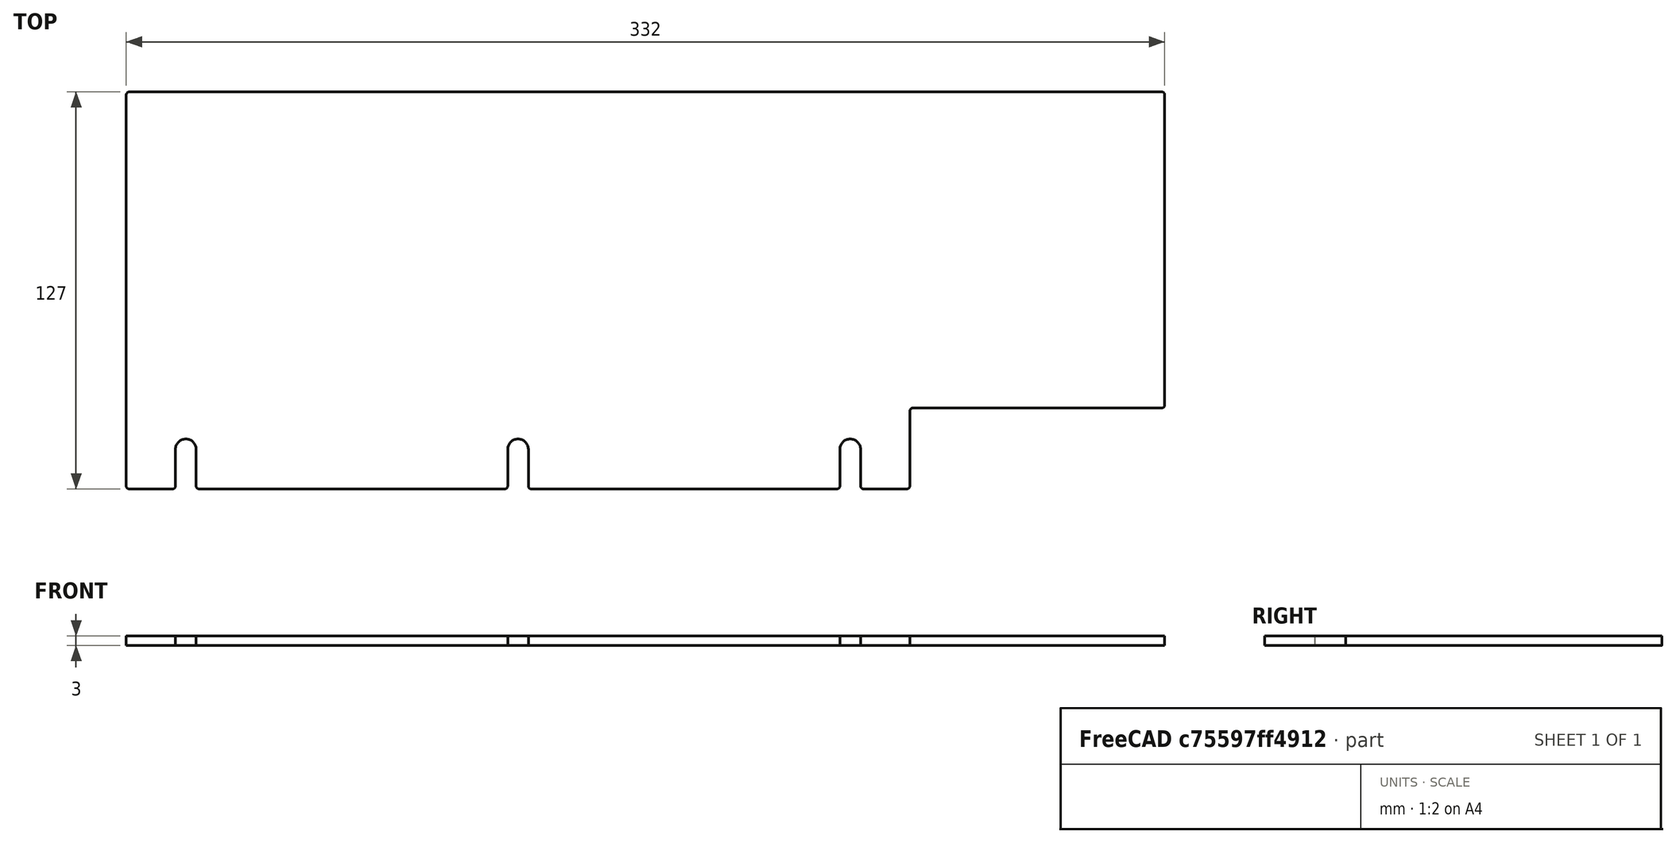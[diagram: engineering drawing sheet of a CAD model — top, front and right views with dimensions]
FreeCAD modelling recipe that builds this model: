
FCSTD DOCUMENT  (FreeCAD 0.21R33675 (Git))
Label: right_wall_front_5in
License: All rights reserved
LicenseURL: http://en.wikipedia.org/wiki/All_rights_reserved
objects: Spreadsheet::Sheet×1, Sketcher::SketchObject×1, PartDesign::Pad×1, PartDesign::Body×1
note: 4 computed .brp shape members not serialized (recipe doc carries the construction recipe); baked Part::Feature solids carry a one-line shape summary decoded from their .brp

FEATURE [Spreadsheet::Sheet] Spreadsheet
  cells = A2='Parameters; A3='ServoOffsetFromCenter; B3(ServoOffsetFromCenter)==-3 in; A4='BeamLength; B4(BeamLength)==18 in; A5='BracketLength; B5(BracketLength)==108.6 mm; A6='DistanceLeftBracketEdgeToDoor; B6(DistanceLeftBracketEdgeToDoor)==82.4999 mm; A7='DistanceRightBracketEdgeToDoor; B7(DistanceRightBracketEdgeToDoor)==23.1001 mm; A8='DoorMargin; B8(DoorMargin)==1 mm; A9='LengthMargin; B9(LengthMargin)==0 mm; A10='LengthLeftBracketEdgeToDoorGap; B10(LengthLeftBracketEdgeToDoorGap)==DistanceLeftBracketEdgeToDoor - DoorMargin; A11='LengthRightBracketEdgeToDoorGap; B11(LengthRightBracketEdgeToDoorGap)==DistanceRightBracketEdgeToDoor - DoorMargin; A12='LengthDoorGap; B12(LengthDoorGap)==BracketLength - LengthLeftBracketEdgeToDoorGap - LengthRightBracketEdgeToDoorGap; A13='BeamLengthMinusBracketLength; B13(BeamLengthMinusBracketLength)==BeamLength - BracketLength; A14='DistanceFrontToDoor; B14(DistanceFrontToDoor)==0.5 * BeamLengthMinusBracketLength + LengthLeftBracketEdgeToDoorGap - ServoOffsetFromCenter; A15='DistanceFrontToBracket; B15(DistanceFrontToBracket)==0.5 * BeamLengthMinusBracketLength - ServoOffsetFromCenter; A16='LengthFrontToDoor; B16(LengthFrontToDoor)==DistanceFrontToDoor - LengthMargin; A17='LengthFrontToBracket; B17(LengthFrontToBracket)==DistanceFrontToBracket - LengthMargin; A18='Height; B18(Height)==5 in; A19='Thickness; B19(Thickness)==3 mm; A20='CutoutMargin; B20(CutoutMargin)==0.5 mm; A21='CutoutHeight; B21(CutoutHeight)==1 in + CutoutMargin; A22='FilletRadius; B22(FilletRadius)==1 mm; A23='MountHoleDiameter; B23(MountHoleDiameter)==0.26 in; A24='MountHoleDistanceFromBottom; B24(MountHoleDistanceFromBottom)==0.5 in; A25='MountHoleSideMargin; B25(MountHoleSideMargin)==0.75 in
FEATURE [Sketcher::SketchObject] Sketch
  FullyConstrained = true
  MapMode = 5
  Support = -> [XY_Plane]
  expr: Constraints[14] = Spreadsheet.FilletRadius
  expr: Constraints[20] = Spreadsheet.Height
  expr: Constraints[43] = Spreadsheet.MountHoleDistanceFromBottom
  expr: Constraints[44] = Spreadsheet.MountHoleDiameter
  expr: Constraints[64] = Spreadsheet.MountHoleSideMargin
  expr: Constraints[7] = Spreadsheet.LengthFrontToDoor
  expr: Constraints[8] = Spreadsheet.LengthFrontToBracket
  expr: Constraints[9] = Spreadsheet.CutoutHeight
  sketch-geometry (50):
    g0: LineSegment StartX=0 StartY=126 StartZ=0 EndX=0 EndY=1 EndZ=0
    g1: LineSegment StartX=1 StartY=0 StartZ=0 EndX=249.5 EndY=0 EndZ=0
    g2: LineSegment StartX=250.5 StartY=1 StartZ=0 EndX=250.5 EndY=24.9 EndZ=0
    g3: LineSegment StartX=251.5 StartY=25.9 StartZ=0 EndX=331 EndY=25.9 EndZ=0
    g4: LineSegment StartX=332 StartY=26.9 StartZ=0 EndX=332 EndY=126 EndZ=0
    g5: LineSegment StartX=331 StartY=127 StartZ=0 EndX=1 EndY=127 EndZ=0
    g6: ArcOfCircle CenterX=1 CenterY=126 CenterZ=0 NormalX=0 NormalY=0 NormalZ=1 AngleXU=0 Radius=1 StartAngle=1.5708 EndAngle=3.14159
    g7: GeomPoint X=0 Y=127 Z=0
    g8: ArcOfCircle CenterX=1 CenterY=1 CenterZ=0 NormalX=0 NormalY=0 NormalZ=1 AngleXU=0 Radius=1 StartAngle=3.14159 EndAngle=4.71239
    g9: GeomPoint X=0 Y=0 Z=0
    g10: ArcOfCircle CenterX=249.5 CenterY=1 CenterZ=0 NormalX=0 NormalY=0 NormalZ=1 AngleXU=0 Radius=1 StartAngle=4.71239 EndAngle=6.28319
    g11: GeomPoint X=250.5 Y=0 Z=0
    g12: ArcOfCircle CenterX=251.5 CenterY=24.9 CenterZ=0 NormalX=0 NormalY=0 NormalZ=1 AngleXU=0 Radius=1 StartAngle=1.5708 EndAngle=3.14159
    g13: GeomPoint X=250.5 Y=25.9 Z=0
    g14: ArcOfCircle CenterX=331 CenterY=26.9 CenterZ=0 NormalX=0 NormalY=0 NormalZ=1 AngleXU=0 Radius=1 StartAngle=4.71239 EndAngle=6.28319
    g15: GeomPoint X=332 Y=25.9 Z=0
    g16: ArcOfCircle CenterX=331 CenterY=126 CenterZ=0 NormalX=0 NormalY=0 NormalZ=1 AngleXU=0 Radius=1 StartAngle=-1.8e-15 EndAngle=1.5708
    g17: GeomPoint X=332 Y=127 Z=0
    g18: GeomPoint X=125.25 Y=0 Z=0
    g19: LineSegment StartX=125.25 StartY=0 StartZ=0 EndX=125.25 EndY=12.7 EndZ=0
    g20: Circle CenterX=125.25 CenterY=12.7 CenterZ=0 NormalX=0 NormalY=0 NormalZ=1 AngleXU=0 Radius=3.302
    g21: LineSegment StartX=19.05 StartY=0 StartZ=0 EndX=19.05 EndY=12.7 EndZ=0
    g22: LineSegment StartX=231.45 StartY=0 StartZ=0 EndX=231.45 EndY=12.7 EndZ=0
    g23: Circle CenterX=19.05 CenterY=12.7 CenterZ=0 NormalX=0 NormalY=0 NormalZ=1 AngleXU=0 Radius=3.302
    g24: Circle CenterX=231.45 CenterY=12.7 CenterZ=0 NormalX=0 NormalY=0 NormalZ=1 AngleXU=0 Radius=3.302
    g25: LineSegment StartX=19.05 StartY=12.7 StartZ=0 EndX=0 EndY=12.7 EndZ=0
    g26: LineSegment StartX=231.45 StartY=12.7 StartZ=0 EndX=250.5 EndY=12.7 EndZ=0
    g27: ArcOfCircle CenterX=19.05 CenterY=12.7 CenterZ=0 NormalX=0 NormalY=0 NormalZ=1 AngleXU=0 Radius=3.302 StartAngle=0 EndAngle=3.14159
    g28: LineSegment StartX=19.05 StartY=12.7 StartZ=0 EndX=22.352 EndY=12.7 EndZ=0
    g29: LineSegment StartX=15.748 StartY=12.7 StartZ=0 EndX=15.748 EndY=1 EndZ=0
    g30: LineSegment StartX=22.352 StartY=12.7 StartZ=0 EndX=22.352 EndY=1 EndZ=0
    g31: ArcOfCircle CenterX=14.748 CenterY=1 CenterZ=0 NormalX=0 NormalY=0 NormalZ=1 AngleXU=0 Radius=1 StartAngle=4.71239 EndAngle=6.28319
    g32: ArcOfCircle CenterX=23.352 CenterY=1 CenterZ=0 NormalX=0 NormalY=0 NormalZ=1 AngleXU=0 Radius=1 StartAngle=3.14159 EndAngle=4.71239
    g33: LineSegment StartX=121.948 StartY=12.7 StartZ=0 EndX=121.948 EndY=1 EndZ=0
    g34: LineSegment StartX=128.552 StartY=12.7 StartZ=0 EndX=128.552 EndY=1 EndZ=0
    g35: ArcOfCircle CenterX=120.948 CenterY=1 CenterZ=0 NormalX=0 NormalY=0 NormalZ=1 AngleXU=0 Radius=1 StartAngle=4.71239 EndAngle=6.28319
    g36: ArcOfCircle CenterX=129.552 CenterY=1 CenterZ=0 NormalX=0 NormalY=0 NormalZ=1 AngleXU=0 Radius=1 StartAngle=3.14159 EndAngle=4.71239
    g37: ArcOfCircle CenterX=125.25 CenterY=12.7 CenterZ=0 NormalX=0 NormalY=0 NormalZ=1 AngleXU=0 Radius=3.302 StartAngle=-7.1e-15 EndAngle=3.14159
    g38: LineSegment StartX=125.25 StartY=12.7 StartZ=0 EndX=121.948 EndY=12.7 EndZ=0
    g39: LineSegment StartX=125.25 StartY=12.7 StartZ=0 EndX=128.552 EndY=12.7 EndZ=0
    g40: LineSegment StartX=228.148 StartY=12.7 StartZ=0 EndX=228.148 EndY=1 EndZ=0
    g41: LineSegment StartX=234.752 StartY=12.7 StartZ=0 EndX=234.752 EndY=1 EndZ=0
    g42: ArcOfCircle CenterX=227.148 CenterY=1 CenterZ=0 NormalX=0 NormalY=0 NormalZ=1 AngleXU=0 Radius=1 StartAngle=4.71239 EndAngle=6.28319
    g43: ArcOfCircle CenterX=235.752 CenterY=1 CenterZ=0 NormalX=0 NormalY=0 NormalZ=1 AngleXU=0 Radius=1 StartAngle=3.14159 EndAngle=4.71239
    g44: ArcOfCircle CenterX=231.45 CenterY=12.7 CenterZ=0 NormalX=0 NormalY=0 NormalZ=1 AngleXU=0 Radius=3.302 StartAngle=1.2e-15 EndAngle=3.14159
    g45: LineSegment StartX=231.45 StartY=12.7 StartZ=0 EndX=228.148 EndY=12.7 EndZ=0
    g46: LineSegment StartX=1 StartY=0 StartZ=0 EndX=14.748 EndY=0 EndZ=0
    g47: LineSegment StartX=23.352 StartY=0 StartZ=0 EndX=120.948 EndY=0 EndZ=0
    g48: LineSegment StartX=129.552 StartY=0 StartZ=0 EndX=227.148 EndY=0 EndZ=0
    g49: LineSegment StartX=235.752 StartY=0 StartZ=0 EndX=249.5 EndY=0 EndZ=0
  constraints (126):
    c: Vertical(g0)
    c: Horizontal(g1)
    c: Vertical(g2)
    c: Horizontal(g3)
    c: Vertical(g4)
    c: Horizontal(g5)
    c: Coincident(g-1,g9)
    c: DistanceX(g7,g17) = 332
    c: DistanceX(g9,g11) = 250.5
    c: DistanceY(g11,g13) = 25.9
    c: PointOnObject(g7,g0)
    c: PointOnObject(g7,g5)
    c: Tangent(g0,g6) = -1.5708
    c: Tangent(g5,g6) = -1.5708
    c: Radius(g6) = 1
    c: PointOnObject(g9,g0)
    c: PointOnObject(g9,g1)
    c: Tangent(g0,g8) = -1.5708
    c: Tangent(g1,g8) = -1.5708
    c: Equal(g8,g6)
    c: DistanceY(g1,g5) = 127
    c: PointOnObject(g11,g1)
    c: PointOnObject(g11,g2)
    c: Tangent(g1,g10) = -1.5708
    c: Tangent(g2,g10) = -1.5708
    c: Equal(g10,g8)
    c: PointOnObject(g13,g2)
    c: PointOnObject(g13,g3)
    c: Tangent(g2,g12) = 1.5708
    c: Tangent(g3,g12) = 1.5708
    c: Equal(g12,g10)
    c: PointOnObject(g15,g3)
    c: PointOnObject(g15,g4)
    c: Tangent(g3,g14) = -1.5708
    c: Tangent(g4,g14) = -1.5708
    c: Equal(g14,g12)
    c: PointOnObject(g17,g5)
    c: PointOnObject(g17,g4)
    c: Tangent(g5,g16) = -1.5708
    c: Tangent(g4,g16) = -1.5708
    c: Equal(g16,g14)
    c: Coincident(g19,g18)
    c: Vertical(g19)
    c: DistanceY(g19,g19) = 12.7
    c: Diameter(g20) = 6.604
    c: Coincident(g19,g20)
    c: Symmetric(g1,g1,g18)
    c: Vertical(g21)
    c: Vertical(g22)
    c: PointOnObject(g21,g1)
    c: PointOnObject(g22,g1)
    c: Equal(g21,g19)
    c: Equal(g19,g22)
    c: Equal(g23,g20)
    c: Equal(g20,g24)
    c: Coincident(g23,g21)
    c: Coincident(g24,g22)
    c: Coincident(g25,g23)
    c: PointOnObject(g25,g0)
    c: Horizontal(g25)
    c: Coincident(g26,g24)
    c: PointOnObject(g26,g2)
    c: Horizontal(g26)
    c: Equal(g25,g26)
    c: DistanceX(g25,g25) = 19.05
    c: Coincident(g27,g21)
    c: PointOnObject(g27,g25)
    c: Coincident(g28,g27)
    c: Coincident(g28,g27)
    c: Horizontal(g28)
    c: PointOnObject(g27,g23)
    c: Coincident(g29,g27)
    c: Vertical(g29)
    c: Coincident(g30,g27)
    c: Vertical(g30)
    c: Equal(g29,g30)
    c: Tangent(g31,g29) = 1.5708
    c: Tangent(g31,g1) = -1.5708
    c: Tangent(g32,g30) = -1.5708
    c: Tangent(g32,g1) = -1.5708
    c: Equal(g31,g8)
    c: Coincident(g33,g37)
    c: Vertical(g33)
    c: Coincident(g34,g37)
    c: Vertical(g34)
    c: Equal(g33,g34)
    c: Tangent(g35,g33) = 1.5708
    c: Tangent(g36,g34) = -1.5708
    c: Coincident(g38,g19)
    c: Horizontal(g38)
    c: Coincident(g39,g19)
    c: Horizontal(g39)
    c: PointOnObject(g38,g20)
    c: PointOnObject(g39,g20)
    c: PointOnObject(g33,g38)
    c: PointOnObject(g33,g20)
    c: PointOnObject(g34,g39)
    c: Coincident(g37,g19)
    c: Tangent(g35,g1) = -1.5708
    c: Tangent(g36,g1) = -1.5708
    c: Equal(g36,g10)
    c: Coincident(g40,g44)
    c: Vertical(g40)
    c: Coincident(g41,g44)
    c: Vertical(g41)
    c: Equal(g40,g41)
    c: Tangent(g42,g40) = 1.5708
    c: Tangent(g43,g41) = -1.5708
    c: Horizontal(g45)
    c: PointOnObject(g40,g45)
    c: PointOnObject(g41,g26)
    c: PointOnObject(g40,g24)
    c: PointOnObject(g45,g24)
    c: Coincident(g45,g22)
    c: Coincident(g44,g22)
    c: Tangent(g42,g1) = -1.5708
    c: Tangent(g43,g1) = -1.5708
    c: Equal(g43,g10)
    c: Coincident(g46,g8)
    c: Coincident(g46,g31)
    c: Coincident(g47,g32)
    c: Coincident(g47,g35)
    c: Coincident(g48,g36)
    c: Coincident(g48,g42)
    c: Coincident(g49,g43)
    c: Coincident(g49,g10)
FEATURE [PartDesign::Pad] Pad
  Direction = (0,0,1)
  Length = 3
  Length2 = 10
  Profile = -> Sketch
  ReferenceAxis = -> Sketch [N_Axis]
  Type = 0
  expr: Length = Spreadsheet.Thickness
FEATURE [PartDesign::Body] Body
  Group = -> [Sketch,Pad]
  Origin = -> Origin
  Tip = -> Pad
